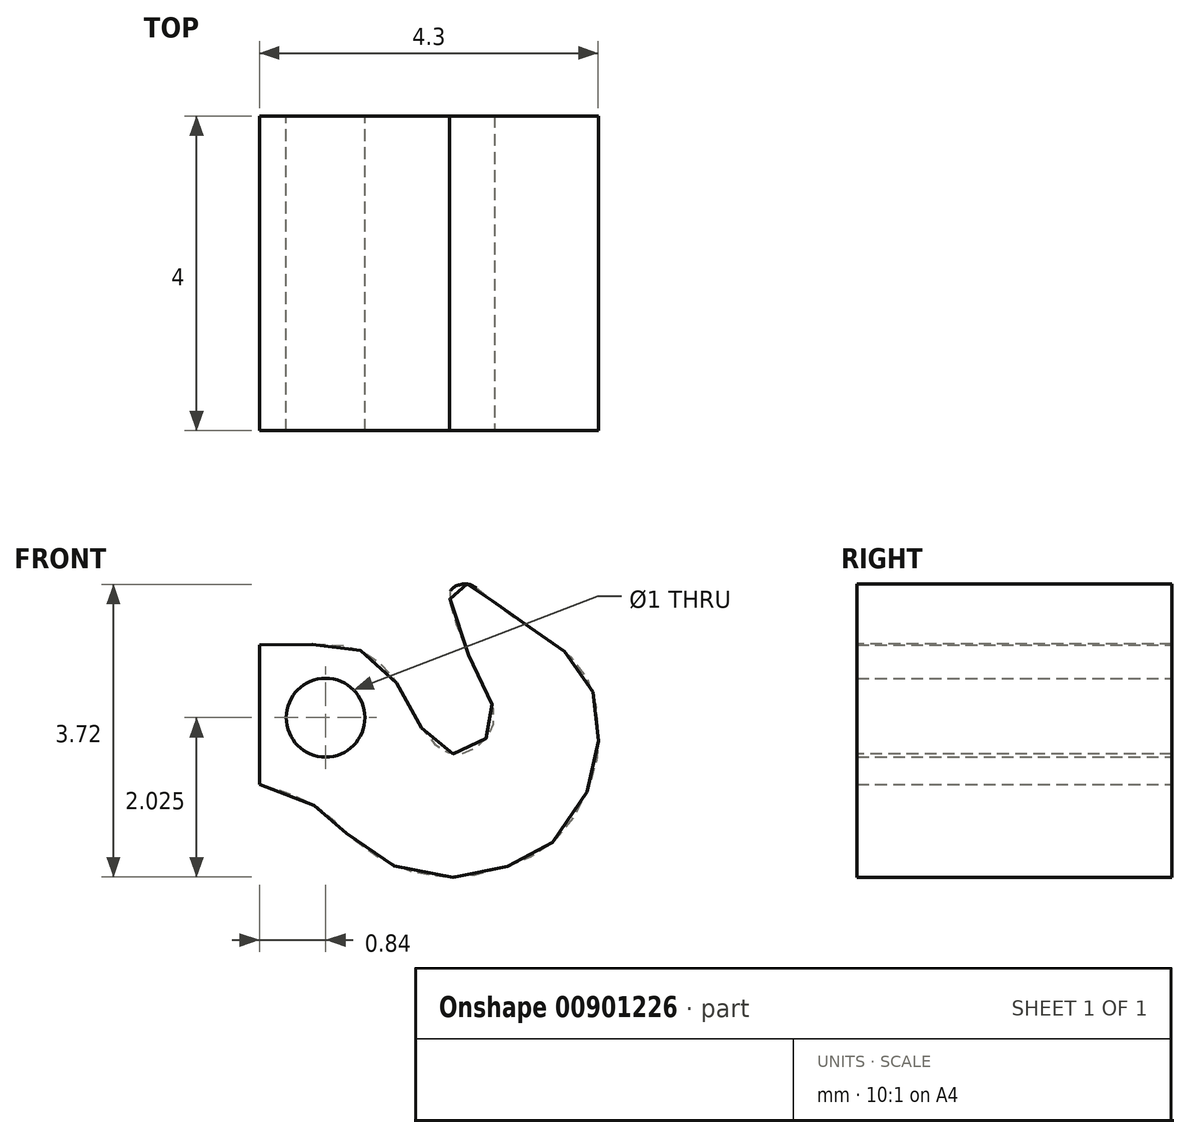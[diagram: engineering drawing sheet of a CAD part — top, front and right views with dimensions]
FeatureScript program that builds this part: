
annotation { "Feature Type Name" : "Feature", "Feature Type Description" : "" }
export const myFeature = defineFeature(function(context is Context, id is Id, definition is map)
    precondition{}
    {
        {
            var Q0;
            Q0=qCreatedBy(makeId("Front.planeOp"),FACE);
            var sketch = newSketch(context, id + "F0", { "sketchPlane" : qUnion([Q0])});
            skFitSpline(sketch, "E0", {"points": [v(-4.43, 2.95) * mm, v(-3.76, 2.96) * mm, v(-3.17, 2.9) * mm, v(-2.73, 2.53) * mm, v(-2.42, 1.97) * mm, v(-2.09, 1.6) * mm, v(-1.78, 1.59) * mm, v(-1.51, 1.81) * mm, v(-1.45, 2.1) * mm, v(-1.68, 2.63) * mm, v(-2, 3.5) * mm, v(-1.97, 3.67) * mm, v(-1.81, 3.72) * mm, v(-1.66, 3.66) * mm, v(-1.4, 3.45) * mm, v(-0.97, 3.15) * mm, v(-0.63, 2.93) * mm, v(-0.25, 2.48) * mm, v(-0.13, 1.87) * mm, v(-0.19, 1.3) * mm, v(-0.64, 0.5) * mm, v(-1.19, 0.17) * mm, v(-1.9, 0) * mm, v(-2.77, 0.17) * mm, v(-3.39, 0.62) * mm, v(-3.71, 0.9) * mm, v(-4.5, 1.2) * mm], "startDerivative": vector(5.27, 0) * mm, "endDerivative": vector(-18.35, 4.13) * mm});
            skCircle(sketch, "E1", {"center": v(-3.59, 2.02) * mm, "radius": 0.5 * mm});
            skLineSegment(sketch, "E2", {"start": v(-4.43, 1.18) * mm, "end": v(-4.43, 2.95) * mm});
            skLineSegment(sketch, "E3", {"start": v(-4.43, 2.95) * mm, "end": v(-4.36, 2.95) * mm});
            skCircle(sketch, "E4", {"center": v(-3.59, 2.02) * mm, "radius": 0.7 * mm});
            skSolve(sketch);
        }
        {
            var Q0;
            {var subQ0=sQuery(id+"F0.wireOp",EDGE,"E0");Q0=makeQuery(id+"F0.imprint","IMPRINT",FACE,{"disambiguationData":[TD([[makeQuery(id+"F0.imprint","IMPRINT",EDGE,{"derivedFrom":subQ0}),-1.0]])]});}
            var Q1;
            Q1=makeQuery(id+"F0.imprint","IMPRINT",FACE,{"disambiguationData":[TD([[makeQuery(id+"F0.imprint","IMPRINT",EDGE,{"derivedFrom":sQuery(id+"F0.wireOp",EDGE,"E1")}),-1.0]])]});
            extrude(context, id + "F1", {"entities" : qUnion([Q0, Q1]), "depth" : 4 * mm, "offsetDistance" : 25 * mm});
        }
    });
